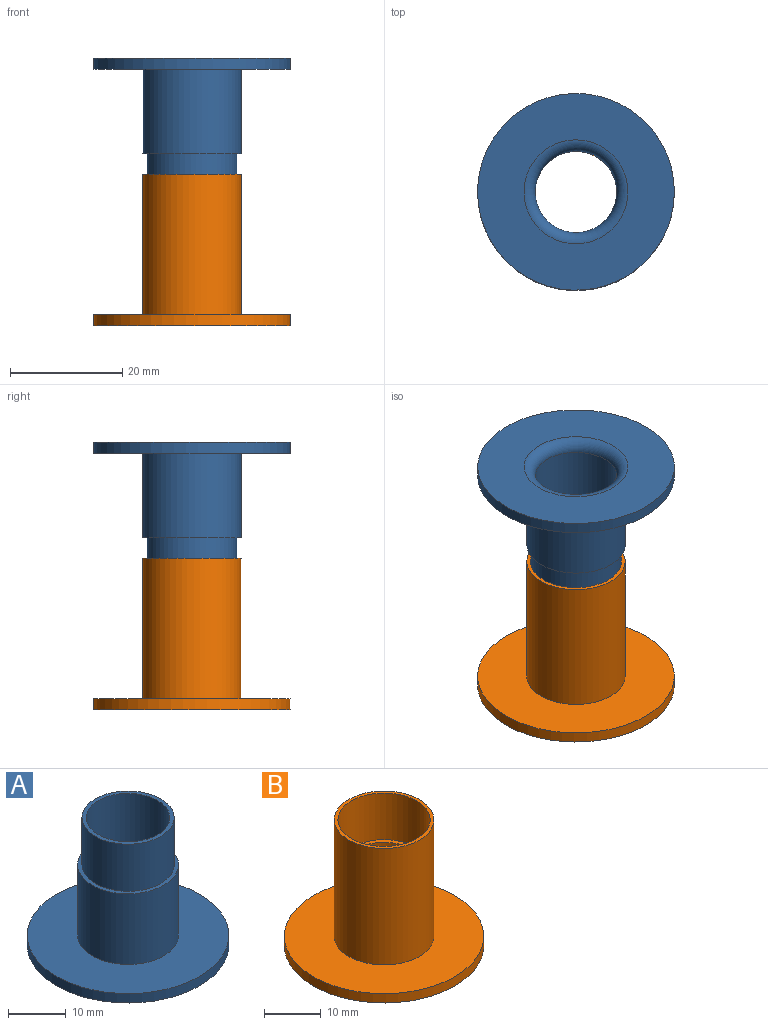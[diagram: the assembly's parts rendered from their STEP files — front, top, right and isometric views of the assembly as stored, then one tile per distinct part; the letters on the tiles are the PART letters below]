
ASSEMBLY  parts=2 mates=1
PART A: 9 faces, bbox 35x35x27 mm
  f0: cylinder r=8.75mm len=17.5mm, axis (0,0,-1), area 824.7mm2, adj f2,f5
  f1: cylinder r=17.5mm len=35mm, axis (0,0,-1), area 219.9mm2, adj f2,f3
  f2: plane 35x35mm, normal (0,0,1), area 721.6mm2, adj f0,f1
  f3: plane 35x35mm, normal (0,0,-1), area 693.3mm2, adj f1,f8
  f4: cylinder r=8mm len=16mm, axis (0,0,1), area 502.7mm2, adj f5,f7
  f5: plane 17.5x17.5mm, normal (0,0,1), area 39.5mm2, adj f0,f4
  f6: cylinder r=7.25mm len=25mm, axis (0,0,-1), area 1138.8mm2, adj f7,f8
  f7: plane 16x16mm, normal (0,0,1), area 35.9mm2, adj f4,f6
  f8: torus R=9.25mm, axis (0,0,1), area 157.5mm2, adj f3,f6
PART B: 9 faces, bbox 35x35x27 mm
  f0: cylinder r=7.25mm len=15mm, axis (0,0,-1), area 683.3mm2, adj f6,f8
  f1: cylinder r=17.5mm len=35mm, axis (0,0,-1), area 219.9mm2, adj f2,f3
  f2: plane 35x35mm, normal (0,0,1), area 721.6mm2, adj f1,f4
  f3: plane 35x35mm, normal (0,0,-1), area 693.3mm2, adj f1,f6
  f4: cylinder r=8.75mm len=25mm, axis (0,0,-1), area 1374.4mm2, adj f2,f5
  f5: plane 17.5x17.5mm, normal (0,0,1), area 34.4mm2, adj f4,f7
  f6: torus R=9.25mm, axis (0,0,1), area 157.5mm2, adj f0,f3
  f7: cylinder r=8.1mm len=16.2mm, axis (0,0,1), area 508.9mm2, adj f5,f8
  f8: plane 16.2x16.2mm, normal (0,0,1), area 41mm2, adj f0,f7
PLACE A rot(axis=(1,0,0),180deg) t=(-30.46,-6.45,58.2)mm
PLACE B rot(axis=(0,0,1),90deg) t=(-30.46,-6.45,10.57)mm
MATE slider A.f4 <-> B.f4  axis (0,0,-1) through (-30.46,-6.45,31.2)mm
